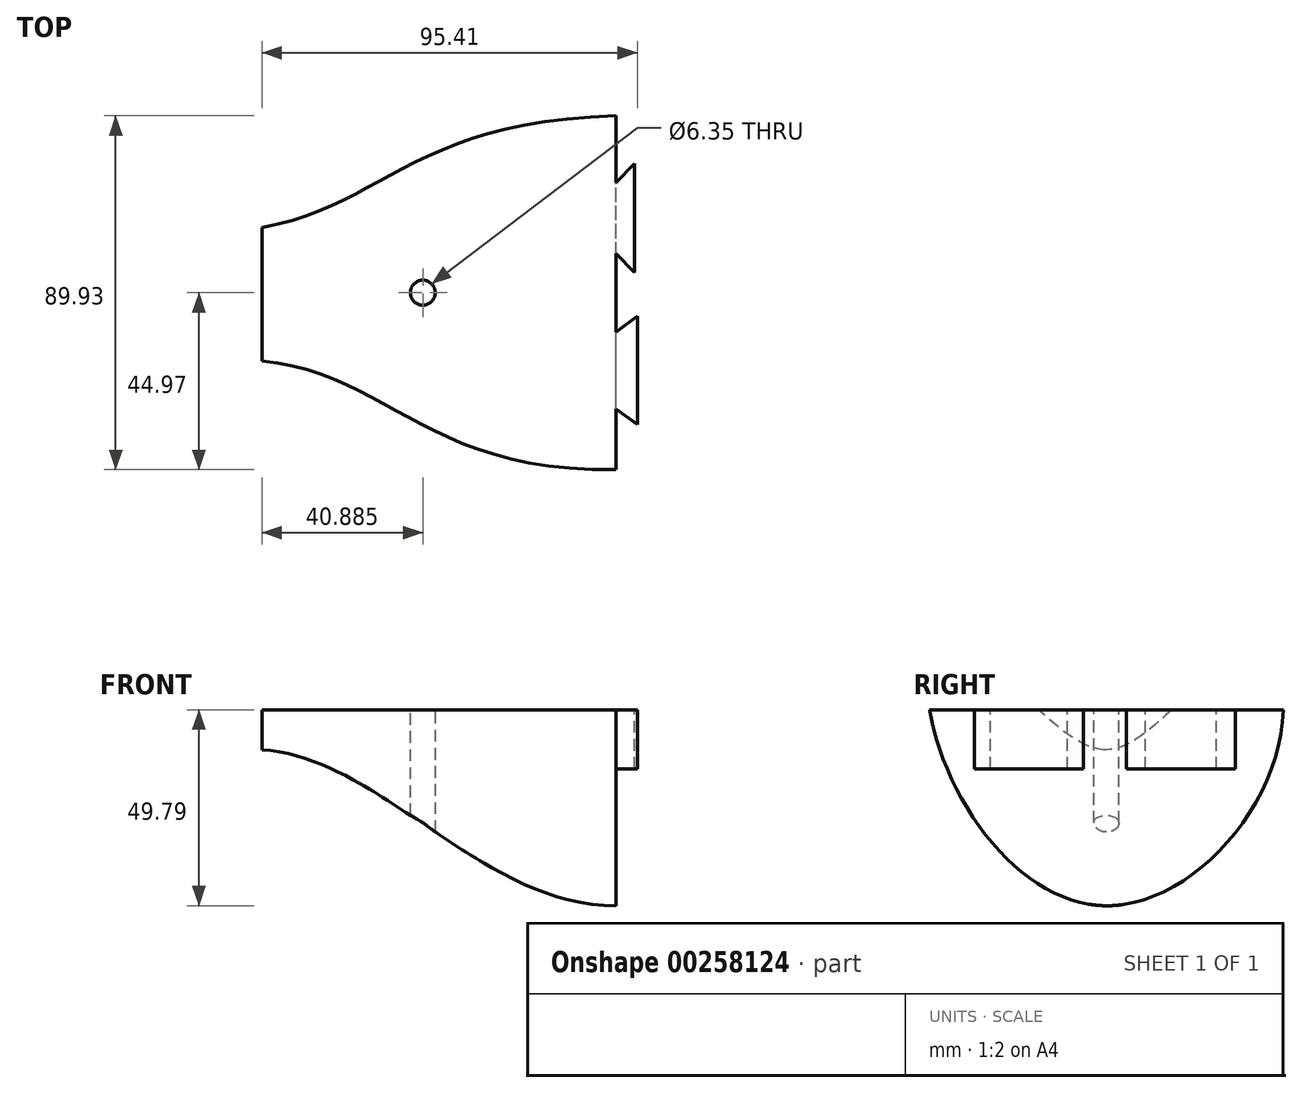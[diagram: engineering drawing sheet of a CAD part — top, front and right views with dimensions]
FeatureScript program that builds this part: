
annotation { "Feature Type Name" : "Feature", "Feature Type Description" : "" }
export const myFeature = defineFeature(function(context is Context, id is Id, definition is map)
    precondition{}
    {
        {
            var Q0;
            Q0=qCreatedBy(makeId("Right.planeOp"),FACE);
            cPlane(context, id + "F0", {"entities" : qUnion([Q0]), "cplaneType" : CPlaneType.OFFSET, "offset" : 89.92 * mm, "width" : 152.4 * mm, "height" : 152.4 * mm});
        }
        {
            var Q0;
            Q0=qCreatedBy(id+"F0.planeOp",FACE);
            var sketch = newSketch(context, id + "F1", { "sketchPlane" : qUnion([Q0])});
            skPoint(sketch, "E0", {"position": v(-44.96, 0) * mm});
            skPoint(sketch, "E1", {"position": v(0, -49.78) * mm});
            skFitSpline(sketch, "E2", {"points": [v(-44.96, 0) * mm, v(0, -49.78) * mm, v(44.96, 0) * mm], "startDerivative": vector(26.57, -148.63) * mm, "endDerivative": vector(5.43, 151.5) * mm});
            skLineSegment(sketch, "E3", {"start": v(-44.96, 0) * mm, "end": v(44.96, 0) * mm});
            skSolve(sketch);
        }
        {
            var Q0;
            Q0=qCreatedBy(makeId("Right.planeOp"),FACE);
            var sketch = newSketch(context, id + "F2", { "sketchPlane" : qUnion([Q0])});
            skPoint(sketch, "E4", {"position": v(16.55, 0) * mm});
            skPoint(sketch, "E5", {"position": v(0, -10.16) * mm});
            skPoint(sketch, "E6", {"position": v(-17.34, 0) * mm});
            skFitSpline(sketch, "E7", {"points": [v(16.55, 0) * mm, v(0, -10.16) * mm, v(-17.34, 0) * mm], "startDerivative": vector(-33.13, -30.57) * mm, "endDerivative": vector(-34.63, 30.4) * mm});
            skLineSegment(sketch, "E8", {"start": v(16.55, 0) * mm, "end": v(-17.34, 0) * mm});
            skSolve(sketch);
        }
        {
            var Q0;
            Q0=qCreatedBy(makeId("Front.planeOp"),FACE);
            var sketch = newSketch(context, id + "F3", { "sketchPlane" : qUnion([Q0])});
            skFitSpline(sketch, "E9", {"points": [v(89.92, -49.78) * mm, v(0, -10.16) * mm], "startDerivative": vector(-101.8, -0.74) * mm, "endDerivative": vector(-90.51, 5.38) * mm});
            skSolve(sketch);
        }
        {
            var Q0;
            Q0=qCreatedBy(makeId("Top.planeOp"),FACE);
            var sketch = newSketch(context, id + "F4", { "sketchPlane" : qUnion([Q0])});
            skFitSpline(sketch, "E10", {"points": [v(89.92, -44.96) * mm, v(0, -17.34) * mm], "startDerivative": vector(-144.93, -2.13) * mm, "endDerivative": vector(-95.21, 8.63) * mm});
            skFitSpline(sketch, "E11", {"points": [v(89.92, 44.96) * mm, v(0, 16.55) * mm], "startDerivative": vector(-154.2, -4.5) * mm, "endDerivative": vector(-93.49, -17.27) * mm});
            skPoint(sketch, "E12", {"position": v(40.96, 0) * mm});
            skSolve(sketch);
        }
        {
            var Q0;
            Q0=makeQuery(id+"F1.imprint","IMPRINT",FACE,{"disambiguationData":[TD([[makeQuery(id+"F1.imprint","IMPRINT",EDGE,{"derivedFrom":sQuery(id+"F1.wireOp",EDGE,"E2")}),1.0]])]});
            var Q1;
            Q1=makeQuery(id+"F2.imprint","IMPRINT",FACE,{"disambiguationData":[TD([[makeQuery(id+"F2.imprint","IMPRINT",EDGE,{"derivedFrom":sQuery(id+"F2.wireOp",EDGE,"E7")}),-1.0]])]});
            var Q2;
            Q2=sQuery(id+"F4.wireOp",EDGE,"E10");
            var Q3;
            Q3=sQuery(id+"F4.wireOp",EDGE,"E11");
            var Q4;
            Q4=sQuery(id+"F3.wireOp",EDGE,"E9");
            loft(context, id + "F5", {"addGuides" : true, "sheetProfilesArray" : [{ "sheetProfileEntities" : qUnion([Q0]) }, { "sheetProfileEntities" : qUnion([Q1]) }], "guidesArray" : [{ "guideEntities" : qUnion([Q2]), "guideDerivativeType" : LoftGuideDerivativeType.DEFAULT, "guideDerivativeMagnitude" : 1 }, { "guideEntities" : qUnion([Q3]), "guideDerivativeType" : LoftGuideDerivativeType.DEFAULT, "guideDerivativeMagnitude" : 1 }, { "guideEntities" : qUnion([Q4]), "guideDerivativeType" : LoftGuideDerivativeType.DEFAULT, "guideDerivativeMagnitude" : 1 }]});
        }
        {
            var Q0;
            Q0=makeQuery(id+"F5.opLoft","SWEPT_FACE",FACE,{"disambiguationData":[OSD([sQuery(id+"F1.wireOp",EDGE,"E3"),sQuery(id+"F2.wireOp",EDGE,"E7"),sQuery(id+"F2.wireOp",EDGE,"E8"),sQuery(id+"F4.wireOp",EDGE,"E10"),sQuery(id+"F4.wireOp",EDGE,"E11")])]});
            var sketch = newSketch(context, id + "F6", { "sketchPlane" : qUnion([Q0])});
            skLineSegment(sketch, "E13", {"start": v(89.92, -29.51) * mm, "end": v(95.41, -33.54) * mm});
            skLineSegment(sketch, "E14", {"start": v(95.41, -33.54) * mm, "end": v(95.41, -5.91) * mm});
            skLineSegment(sketch, "E15", {"start": v(95.41, -5.91) * mm, "end": v(89.92, -9.93) * mm});
            skSolve(sketch);
        }
        {
            var Q0;
            {var subQ0=sQuery(id+"F6.wireOp",EDGE,"E13");Q0=makeQuery(id+"F6.imprint","IMPRINT",FACE,{"disambiguationData":[TD([[makeQuery(id+"F6.imprint","IMPRINT",EDGE,{"derivedFrom":subQ0}),1.0]])]});}
            extrude(context, id + "F7", {"entities" : qUnion([Q0]), "operationType" : NewBodyOperationType.ADD, "oppositeDirection" : true, "depth" : 15 * mm});
        }
        {
            var Q0;
            {var subQ0=sQuery(id+"F4.wireOp",EDGE,"E11");var subQ1=sQuery(id+"F4.wireOp",EDGE,"E10");var subQ2=sQuery(id+"F1.wireOp",EDGE,"E3");Q0=makeQuery(id+"F7.boolean.opBoolean","MERGE",FACE,{"derivedFrom":[makeQuery(id+"F5.opLoft","SWEPT_FACE",FACE,{"disambiguationData":[OSD([subQ2,sQuery(id+"F2.wireOp",EDGE,"E7"),sQuery(id+"F2.wireOp",EDGE,"E8"),subQ1,subQ0])]}),makeQuery(id+"F7.opExtrude","CAP_FACE",FACE,{"disambiguationData":[OSD([subQ2,subQ1,subQ0,sQuery(id+"F6.wireOp",EDGE,"E13"),sQuery(id+"F6.wireOp",EDGE,"E14"),sQuery(id+"F6.wireOp",EDGE,"E15")])],"isStart":true})]});}
            var sketch = newSketch(context, id + "F8", { "sketchPlane" : qUnion([Q0])});
            skLineSegment(sketch, "E16", {"start": v(89.92, 27.97) * mm, "end": v(94.73, 32.78) * mm});
            skLineSegment(sketch, "E17", {"start": v(94.73, 32.78) * mm, "end": v(94.73, 5.12) * mm});
            skLineSegment(sketch, "E18", {"start": v(94.73, 5.12) * mm, "end": v(89.92, 9.93) * mm});
            skSolve(sketch);
        }
        {
            var Q0;
            {var subQ0=sQuery(id+"F8.wireOp",EDGE,"E16");Q0=makeQuery(id+"F8.imprint","IMPRINT",FACE,{"disambiguationData":[TD([[makeQuery(id+"F8.imprint","IMPRINT",EDGE,{"derivedFrom":subQ0}),-1.0]])]});}
            extrude(context, id + "F9", {"entities" : qUnion([Q0]), "operationType" : NewBodyOperationType.ADD, "oppositeDirection" : true, "depth" : 15 * mm});
        }
        {
            var Q0;
            {var subQ0=sQuery(id+"F4.wireOp",EDGE,"E11");var subQ1=sQuery(id+"F4.wireOp",EDGE,"E10");var subQ2=sQuery(id+"F1.wireOp",EDGE,"E3");Q0=makeQuery(id+"F9.boolean.opBoolean","MERGE",FACE,{"derivedFrom":[makeQuery(id+"F7.boolean.opBoolean","MERGE",FACE,{"derivedFrom":[makeQuery(id+"F5.opLoft","SWEPT_FACE",FACE,{"disambiguationData":[OSD([subQ2,sQuery(id+"F2.wireOp",EDGE,"E7"),sQuery(id+"F2.wireOp",EDGE,"E8"),subQ1,subQ0])]}),makeQuery(id+"F7.opExtrude","CAP_FACE",FACE,{"disambiguationData":[OSD([subQ2,subQ1,subQ0,sQuery(id+"F6.wireOp",EDGE,"E13"),sQuery(id+"F6.wireOp",EDGE,"E14"),sQuery(id+"F6.wireOp",EDGE,"E15")])],"isStart":true})]}),makeQuery(id+"F9.opExtrude","CAP_FACE",FACE,{"disambiguationData":[OSD([subQ2,subQ1,subQ0,sQuery(id+"F8.wireOp",EDGE,"E16"),sQuery(id+"F8.wireOp",EDGE,"E17"),sQuery(id+"F8.wireOp",EDGE,"E18")])],"isStart":true})]});}
            var sketch = newSketch(context, id + "F10", { "sketchPlane" : qUnion([Q0])});
            skCircle(sketch, "E19", {"center": v(40.89, 0) * mm, "radius": 5.08 * mm});
            skSolve(sketch);
        }
        {
            var Q0;
            Q0=sQuery(id+"F10.wireOp",VERTEX,"E19.center");
            var Q1;
            Q1=makeQuery(id+"F5.opLoft","SWEPT_BODY",BODY,{"disambiguationData":[OSD([makeQuery(id+"F1.imprint","IMPRINT",FACE,{"disambiguationData":[TD([[makeQuery(id+"F1.imprint","IMPRINT",EDGE,{"derivedFrom":sQuery(id+"F1.wireOp",EDGE,"E2")}),1.0]])]}),makeQuery(id+"F2.imprint","IMPRINT",FACE,{"disambiguationData":[TD([[makeQuery(id+"F2.imprint","IMPRINT",EDGE,{"derivedFrom":sQuery(id+"F2.wireOp",EDGE,"E7")}),-1.0]])]}),sQuery(id+"F3.wireOp",EDGE,"E9"),sQuery(id+"F4.wireOp",EDGE,"E10"),sQuery(id+"F4.wireOp",EDGE,"E11")])]});
            hole(context, id + "F11", {"style" : HoleStyle.SIMPLE, "endStyle" : HoleEndStyle.THROUGH, "holeDiameter" : 6.35 * mm, "tappedDepth" : 12.7 * mm, "tapClearance" : 3, "locations" : qUnion([Q0]), "scope" : qUnion([Q1])});
        }
    });
